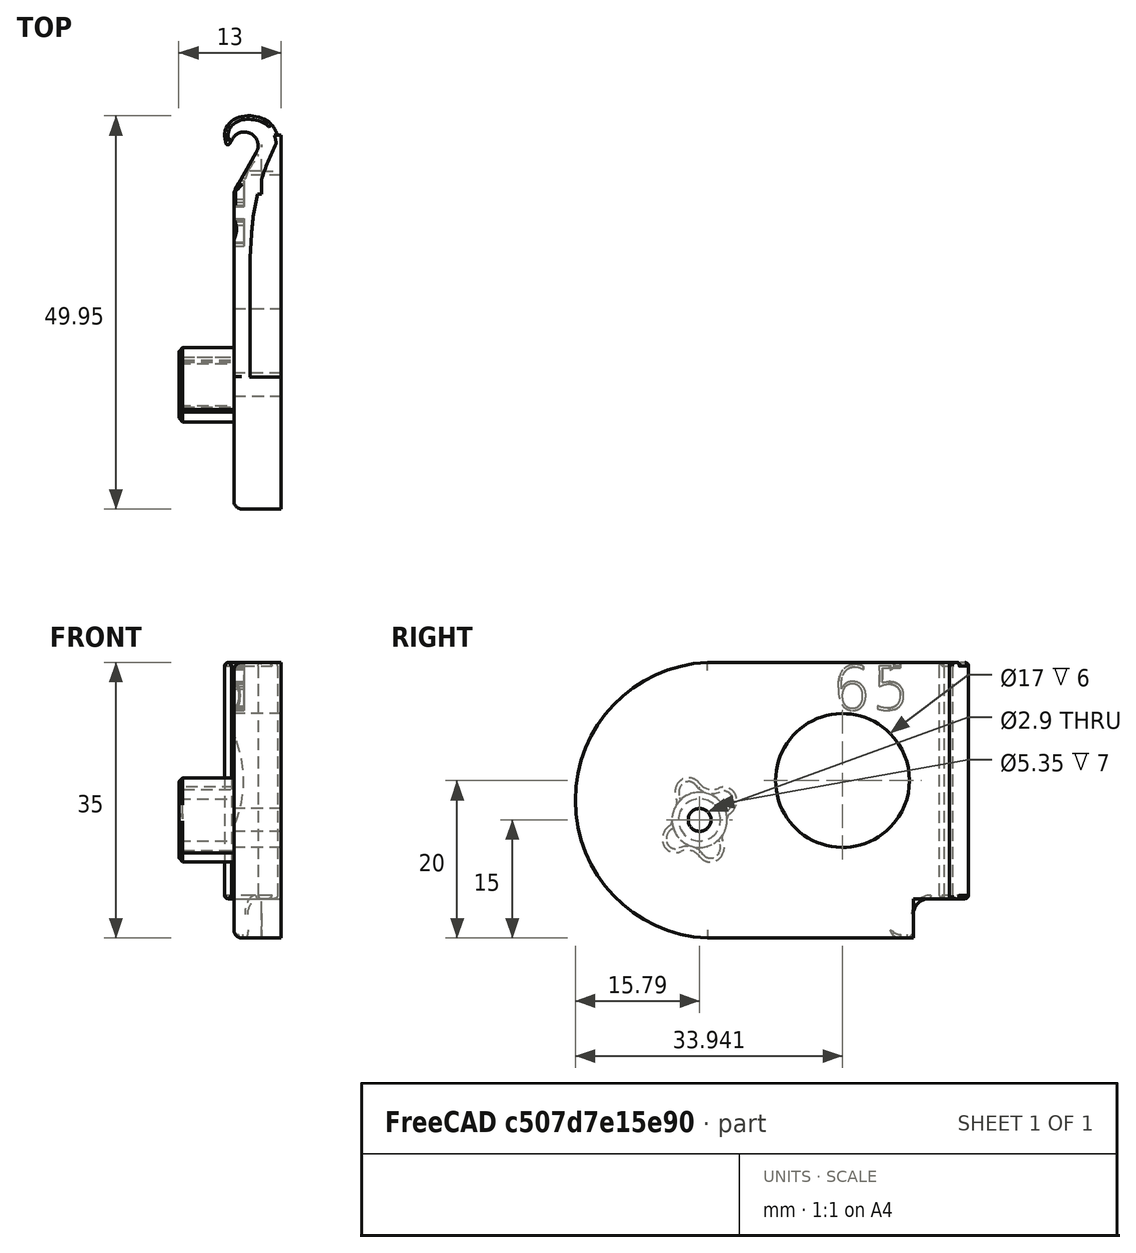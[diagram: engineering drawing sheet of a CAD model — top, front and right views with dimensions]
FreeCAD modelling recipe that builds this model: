
FCSTD DOCUMENT  (FreeCAD 0.18R)
Label: hinge-right-165deg-flat
License: All rights reserved
LicenseURL: http://en.wikipedia.org/wiki/All_rights_reserved
objects: App::FeaturePython×6, Part::FeaturePython×2, Part::Part2DObjectPython×1, Part::Extrusion×1, Part::Cut×1
note: 5 computed .brp shape members not serialized (recipe doc carries the construction recipe); baked Part::Feature solids carry a one-line shape summary decoded from their .brp

FEATURE [Part::FeaturePython] pillar_base_001  label="pillar-base_001"  # a2plus imported part (geometry in sourceFile) (typed FeaturePython)
  Placement = pos=(0.000608724,-57.9617,21.0906) rot=(-1,0,0;0.697957rad)
  a2p_Version = V0.1
  fixedPosition = false
  objectType = a2pPart
  sourceFile = ./parts/pillar-base.fcstd
  subassemblyImport = false
  timeLastImport = 1.60452e+09
  updateColors = true
FEATURE [Part::Part2DObjectPython] ShapeString  # Draft 2D object (typed FeaturePython)
  FontFile = <path>
  Placement = pos=(1.61,10.5,29) rot=(0.57735,-0.57735,-0.57735;2.0944rad)
  Size = 6
  String = 65
  Tracking = 0
FEATURE [Part::Extrusion] Extrude
  Base = -> ShapeString
  Dir = (-1,0,0)
  DirMode = 2
  FaceMakerClass = Part::FaceMakerBullseye
  LengthFwd = 3.5
  LengthRev = 0
  Placement = pos=(0,0,0) rot=(0,0,1;3.14159rad)
  Solid = false
  Symmetric = false
FEATURE [Part::FeaturePython] bracket_right_flat_001  label="bracket-right-flat_001"  # a2plus imported part (geometry in sourceFile) (typed FeaturePython)
  Placement = pos=(0,0,0) rot=(0,0,1;3.14159rad)
  a2p_Version = V0.1
  fixedPosition = true
  objectType = a2pPart
  sourceFile = ./parts/bracket-right-flat.fcstd
  subassemblyImport = false
  timeLastImport = 1.60489e+09
  updateColors = true
FEATURE [App::FeaturePython] axisCoincident_001  label="axisCoincident_001__bracket-right-flat_001"  # a2plus constraint (typed FeaturePython)
  Object1 = pillar_base_001
  Object2 = bracket_right_flat_001
  ParentTreeObject = -> pillar_base_001
  SubElement1 = Face17
  SubElement2 = Face31
  Suppressed = false
  Type = axial
  directionConstraint = 1
  lockRotation = false
FEATURE [App::FeaturePython] axisCoincident_001_mirror  label="axisCoincident_001__pillar-base_001"  # a2plus constraint (typed FeaturePython)
  Object1 = pillar_base_001
  Object2 = bracket_right_flat_001
  ParentTreeObject = -> bracket_right_flat_001
  SubElement1 = Face17
  SubElement2 = Face31
  Suppressed = false
  Type = axial
  directionConstraint = 1
  lockRotation = false
FEATURE [App::FeaturePython] planeCoincident_001  label="planeCoincident_001__bracket-right-flat_001"  # a2plus constraint (typed FeaturePython)
  Object1 = pillar_base_001
  Object2 = bracket_right_flat_001
  ParentTreeObject = -> pillar_base_001
  SubElement1 = Face1
  SubElement2 = Face57
  Suppressed = false
  Type = plane
  directionConstraint = 1
  offset = 0
FEATURE [App::FeaturePython] planeCoincident_001_mirror  label="planeCoincident_001__pillar-base_001"  # a2plus constraint (typed FeaturePython)
  Object1 = pillar_base_001
  Object2 = bracket_right_flat_001
  ParentTreeObject = -> bracket_right_flat_001
  SubElement1 = Face1
  SubElement2 = Face57
  Suppressed = false
  Type = plane
  directionConstraint = 1
  offset = 0
FEATURE [Part::Cut] Cut
  Base = -> bracket_right_flat_001
  Tool = -> Extrude
FEATURE [App::FeaturePython] axisCoincident_001_mirror001  label="axisCoincident_001__bracket-right-flat_001_"  # a2plus constraint (typed FeaturePython)
  Object1 = pillar_base_001
  Object2 = bracket_right_flat_001
  ParentTreeObject = -> pillar_base_001
  SubElement1 = Face17
  SubElement2 = Face31
  Suppressed = false
  Type = axial
  directionConstraint = 1
  lockRotation = false
FEATURE [App::FeaturePython] planeCoincident_001_mirror001  label="planeCoincident_001__bracket-right-flat_001_"  # a2plus constraint (typed FeaturePython)
  Object1 = pillar_base_001
  Object2 = bracket_right_flat_001
  ParentTreeObject = -> pillar_base_001
  SubElement1 = Face1
  SubElement2 = Face57
  Suppressed = false
  Type = plane
  directionConstraint = 1
  offset = 0
note: 1 file-system path scrubbed to <path> (originals preserved in the JSON sidecar)
